# Revit family: Amplifier-Power-Q-SYS-Networkable-SPA-Qf-4 Channel-Tandem
name_source: partatom
category: Communication Devices
units: mm (PartAtom-declared; Revit-internal decimal feet)

## family parameters
Cut with Voids When Loaded = No
Host = Face
Maintain Annotation Orientation = No
OmniClass Number = 23.85.10.14
OmniClass Title = Visual Information Systems
Part Type = Normal
Room Calculation Point = No
Round Connector Dimension = Use Diameter
Shared = No

## types (1)
- SPA-Qf x 2
    Apparent Load = 1000 VA
    Body Height = 30.5 mm  [stored 0.100066 ft]
    Body Material = Paint - Q-SYS - Black
    Body Offset = 0 mm  [stored 0 ft]
    Body Width = 446 mm  [stored 1.46325 ft]
    Bracket Depth = 80 mm  [stored 0.262467 ft]
    Default Elevation = 1219.2 mm  [stored 4 ft]
    Depth = 287 mm  [stored 0.941601 ft]
    Description = Tandem network amplifiers for Q-SYS platform
    Frame Depth = 2 mm  [stored 0.00656168 ft]
    Frame Height = 30.5 mm  [stored 0.100066 ft]
    Grille Material = Paint - Q-SYS - Black Mesh
    Height = 44 mm  [stored 0.144357 ft]
    Highlight Material = Plastic - Q-SYS - Black
    IQ Category = Amplifier
    LED Material = Plastic - Q-SYS - LED Blue
    Left Bracket = Yes
    Length 1 = 18.5 mm  [stored 0.0606955 ft]
    Length 2 = 10 mm  [stored 0.0328084 ft]
    Length 3 = 3 mm  [stored 0.00984252 ft]
    Load Classification = Other
    Manufacturer = Q-SYS
    Manufacturer URL = https://www.qsys.com
    Minimum Circuit Amps = 12 A
    Model = SPA-Qf x 2
    Number of Poles = 2
    Power Factor = 0.9
    Product Documentation Link = https://www.qsys.com
    Product Page URL = https://www.qsys.com
    Right Bracket = Yes
    Type Comments = 4 Channel Surface Mounted x 2
    URL = https://www.qsys.com
    Voltage = 75 V
    Weight = 12.80 lbm
    Weight Dimensional = 12.8
    Weight Product = 12.8
    Width = 483 mm

note: [stored X ft] marks values corroborated as IEEE doubles in the binary element streams (Revit-internal decimal feet)

## geometry (parser evidence)
native form markers: Sweep x4
no freeform markers — native parametric forms only
